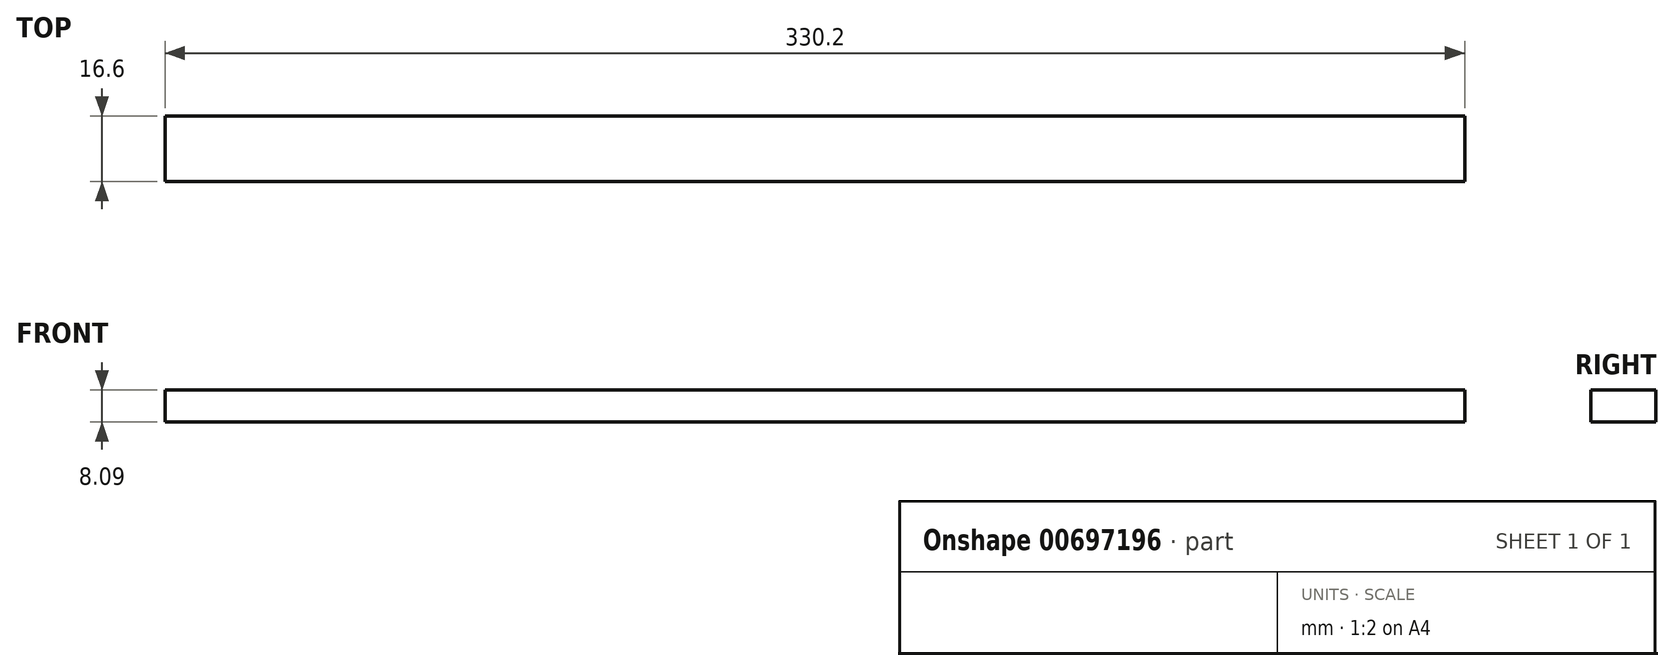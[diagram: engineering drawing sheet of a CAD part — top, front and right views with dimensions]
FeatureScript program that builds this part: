
annotation { "Feature Type Name" : "Feature", "Feature Type Description" : "" }
export const myFeature = defineFeature(function(context is Context, id is Id, definition is map)
    precondition{}
    {
        {
            var Q0;
            Q0=qCreatedBy(makeId("Right.planeOp"),FACE);
            var sketch = newSketch(context, id + "F0", { "sketchPlane" : qUnion([Q0])});
            skCircle(sketch, "E0", {"center": v(0, 0) * mm, "radius": 14.57 * mm});
            skSolve(sketch);
        }
        {
            var Q0;
            Q0=makeQuery(id+"F0.imprint","IMPRINT",FACE,{"disambiguationData":[TD([[makeQuery(id+"F0.imprint","IMPRINT",EDGE,{"derivedFrom":sQuery(id+"F0.wireOp",EDGE,"E0")}),1.0]])]});
            var sketch = newSketch(context, id + "F1", { "sketchPlane" : qUnion([Q0])});
            skLineSegment(sketch, "E1.bottom", {"start": v(-7.68, 0) * mm, "end": v(8.92, 0) * mm});
            skLineSegment(sketch, "E1.top", {"start": v(-7.68, -8.1) * mm, "end": v(8.92, -8.1) * mm});
            skLineSegment(sketch, "E1.left", {"start": v(-7.68, 0) * mm, "end": v(-7.68, -8.1) * mm});
            skLineSegment(sketch, "E1.right", {"start": v(8.92, 0) * mm, "end": v(8.92, -8.1) * mm});
            skSolve(sketch);
        }
        {
            var Q0;
            Q0 = qSketchRegion(id + "F1", true);
            extrude(context, id + "F2", {"entities" : qUnion([Q0]), "depth" : 330.2 * mm, "offsetDistance" : 25.4 * mm});
        }
    });
